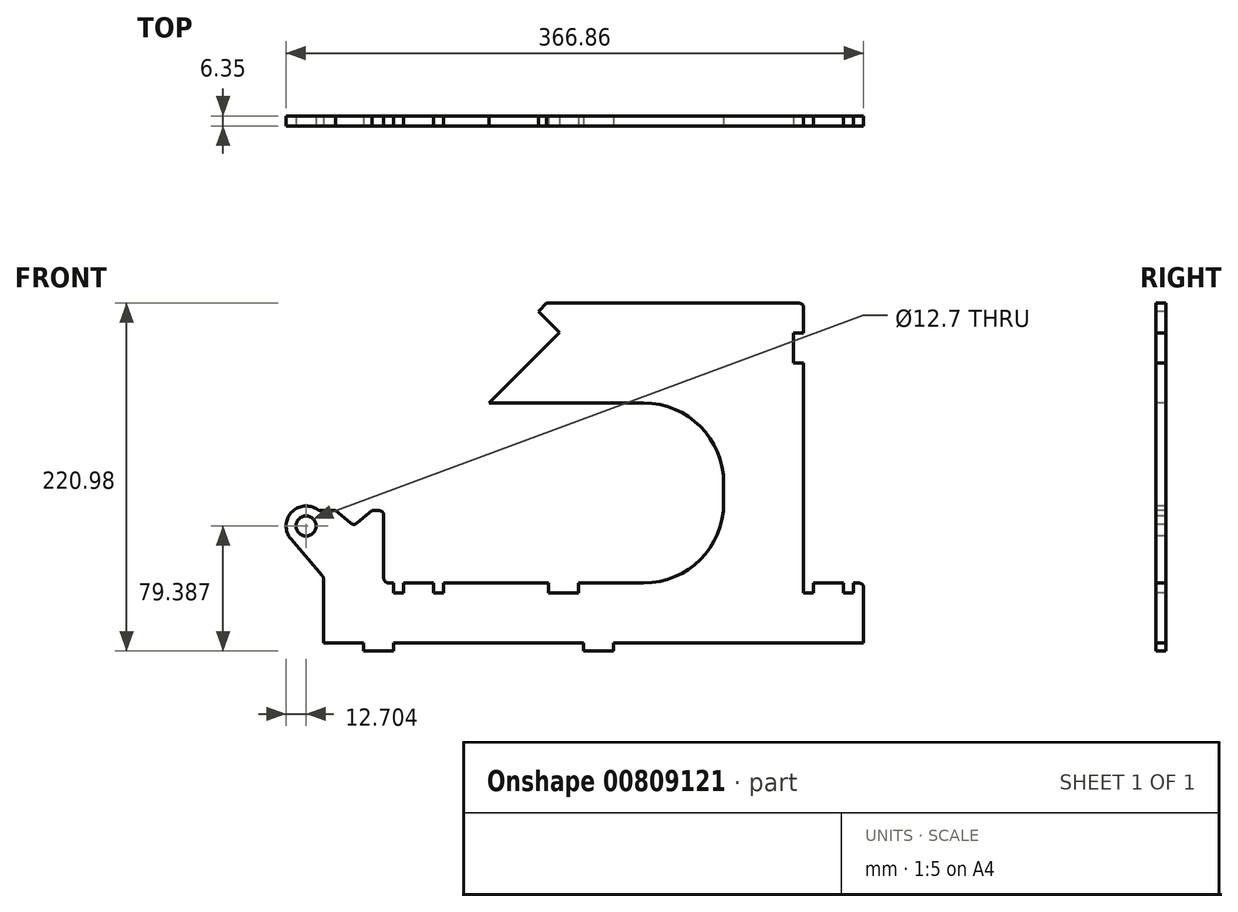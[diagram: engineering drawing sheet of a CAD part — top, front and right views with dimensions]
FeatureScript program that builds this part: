
annotation { "Feature Type Name" : "Feature", "Feature Type Description" : "" }
export const myFeature = defineFeature(function(context is Context, id is Id, definition is map)
    precondition{}
    {
        {
            var Q0;
            Q0=qCreatedBy(makeId("Front.planeOp"),FACE);
            var sketch = newSketch(context, id + "F0", { "sketchPlane" : qUnion([Q0])});
            skCircle(sketch, "E0", {"center": v(-91.4, -60.1) * mm, "radius": 6.35 * mm});
            skArc(sketch, "E1", {"start": v(-83.36, -50.27) * mm, "mid": v(-100.48, -51.22) * mm, "end": v(-101.06, -68.36) * mm});
            skLineSegment(sketch, "E2", {"start": v(-101.06, -68.36) * mm, "end": v(-80.15, -92.8) * mm});
            skLineSegment(sketch, "E3.trimOffspring", {"start": v(-80.15, -92.8) * mm, "end": v(-80.15, -134.4) * mm});
            skCircle(sketch, "E4", {"center": v(-61.1, -45.5) * mm, "radius": 11.11 * mm, "construction": true});
            skLineSegment(sketch, "E5.0", {"start": v(-83.36, -50.27) * mm, "end": v(-72.7, -50.27) * mm});
            skLineSegment(sketch, "E6", {"start": v(-42.05, -50.27) * mm, "end": v(-42.05, -96.3) * mm});
            skLineSegment(sketch, "E7.trimOffspring", {"start": v(-49.48, -50.27) * mm, "end": v(-42.05, -50.27) * mm});
            skPoint(sketch, "E8.orphan", {"position": v(-61.1, -63.47) * mm});
            skLineSegment(sketch, "E9.0", {"start": v(-72.7, -50.27) * mm, "end": v(-61.1, -60.02) * mm});
            skLineSegment(sketch, "E10.0", {"start": v(-49.48, -50.27) * mm, "end": v(-61.1, -60.02) * mm});
            skLineSegment(sketch, "E11", {"start": v(-68.24, -54.02) * mm, "end": v(-61.1, -45.5) * mm, "construction": true});
            skLineSegment(sketch, "E12", {"start": v(-53.95, -54.02) * mm, "end": v(-61.1, -45.5) * mm, "construction": true});
            skLineSegment(sketch, "E13.0", {"start": v(-42.05, -96.3) * mm, "end": v(-35.7, -96.3) * mm});
            skLineSegment(sketch, "E14.0", {"start": v(-80.15, -134.4) * mm, "end": v(262.75, -134.4) * mm});
            skLineSegment(sketch, "E15", {"start": v(-61.1, -45.5) * mm, "end": v(-34.5, -18.92) * mm, "construction": true});
            skLineSegment(sketch, "E16.0", {"start": v(-60.66, -29.36) * mm, "end": v(50.47, 81.77) * mm, "construction": true});
            skLineSegment(sketch, "E17", {"start": v(-61.1, -45.5) * mm, "end": v(-68.95, -37.65) * mm});
            skLineSegment(sketch, "E18.0", {"start": v(-53.24, -37.65) * mm, "end": v(-61.1, -29.8) * mm, "construction": true});
            skLineSegment(sketch, "E19.0", {"start": v(69.55, 62.69) * mm, "end": v(56.08, 76.16) * mm});
            skLineSegment(sketch, "E20.0", {"start": v(-52.8, -37.22) * mm, "end": v(-60.66, -29.36) * mm, "construction": true});
            skLineSegment(sketch, "E21.0", {"start": v(-63.34, -43.26) * mm, "end": v(50.52, 70.6) * mm, "construction": true});
            skLineSegment(sketch, "E22.0", {"start": v(173.85, -32.8) * mm, "end": v(173.85, -45.5) * mm});
            skLineSegment(sketch, "E23.0", {"start": v(61.41, 81.5) * mm, "end": v(224.65, 81.5) * mm});
            skLineSegment(sketch, "E24.0", {"start": v(6.9, 18) * mm, "end": v(24.85, 18) * mm, "construction": true});
            skLineSegment(sketch, "E25.0", {"start": v(224.65, 81.5) * mm, "end": v(224.65, 62.44) * mm});
            skLineSegment(sketch, "E26.0", {"start": v(-23.62, -12.52) * mm, "end": v(6.9, 18) * mm, "construction": true});
            skLineSegment(sketch, "E27.0", {"start": v(-23.62, -12.52) * mm, "end": v(-28.11, -8.03) * mm, "construction": true});
            skLineSegment(sketch, "E28", {"start": v(56.08, 76.16) * mm, "end": v(61.41, 81.5) * mm});
            skLineSegment(sketch, "E29", {"start": v(6.9, 18) * mm, "end": v(60.57, 71.67) * mm, "construction": true});
            skLineSegment(sketch, "E30.top", {"start": v(-35.7, -102.66) * mm, "end": v(-29.35, -102.66) * mm});
            skLineSegment(sketch, "E30.left", {"start": v(-35.7, -96.3) * mm, "end": v(-35.7, -102.66) * mm});
            skLineSegment(sketch, "E30.right", {"start": v(-29.35, -96.3) * mm, "end": v(-29.35, -102.66) * mm});
            skLineSegment(sketch, "E31.bottom", {"start": v(-10.3, -102.66) * mm, "end": v(-3.95, -102.66) * mm});
            skLineSegment(sketch, "E31.left", {"start": v(-10.3, -102.66) * mm, "end": v(-10.3, -96.3) * mm});
            skLineSegment(sketch, "E31.right", {"start": v(-3.95, -102.66) * mm, "end": v(-3.95, -96.3) * mm});
            skLineSegment(sketch, "E32.trimOffspring", {"start": v(-29.35, -96.3) * mm, "end": v(-10.3, -96.3) * mm});
            skLineSegment(sketch, "E33.trimOffspring", {"start": v(-3.95, -96.3) * mm, "end": v(123.05, -96.3) * mm});
            skLineSegment(sketch, "E34.top", {"start": v(224.65, 62.44) * mm, "end": v(218.3, 62.44) * mm});
            skLineSegment(sketch, "E35.bottom", {"start": v(218.3, 43.4) * mm, "end": v(224.65, 43.4) * mm});
            skLineSegment(sketch, "E35.left", {"start": v(218.3, 62.44) * mm, "end": v(218.3, 43.4) * mm});
            skLineSegment(sketch, "E36.trimOffspring", {"start": v(224.65, 43.4) * mm, "end": v(224.65, -102.66) * mm});
            skLineSegment(sketch, "E37.0", {"start": v(262.75, -96.3) * mm, "end": v(262.75, -134.4) * mm});
            skLineSegment(sketch, "E38.trimOffspring", {"start": v(231, -96.3) * mm, "end": v(250.05, -96.3) * mm});
            skLineSegment(sketch, "E39.top", {"start": v(224.65, -102.66) * mm, "end": v(231, -102.66) * mm});
            skLineSegment(sketch, "E39.right", {"start": v(231, -96.3) * mm, "end": v(231, -102.66) * mm});
            skLineSegment(sketch, "E40.top", {"start": v(250.05, -102.66) * mm, "end": v(256.4, -102.66) * mm});
            skLineSegment(sketch, "E40.left", {"start": v(250.05, -96.3) * mm, "end": v(250.05, -102.66) * mm});
            skLineSegment(sketch, "E40.right", {"start": v(256.4, -96.3) * mm, "end": v(256.4, -102.66) * mm});
            skLineSegment(sketch, "E41.trimOffspring", {"start": v(256.4, -96.3) * mm, "end": v(262.75, -96.3) * mm});
            skPoint(sketch, "E42.visualSharp", {"position": v(173.85, 18) * mm});
            skArc(sketch, "E42.filletArc", {"start": v(173.85, -32.8) * mm, "mid": v(158.97, 3.11) * mm, "end": v(123.05, 18) * mm});
            skPoint(sketch, "E43.visualSharp", {"position": v(173.85, -96.3) * mm});
            skArc(sketch, "E43.filletArc", {"start": v(123.05, -96.3) * mm, "mid": v(158.97, -81.43) * mm, "end": v(173.85, -45.5) * mm});
            skLineSegment(sketch, "E44.bottom", {"start": v(62.73, -102.66) * mm, "end": v(81.78, -102.66) * mm});
            skLineSegment(sketch, "E44.top", {"start": v(62.73, -96.3) * mm, "end": v(81.78, -96.3) * mm});
            skLineSegment(sketch, "E44.left", {"start": v(62.73, -102.66) * mm, "end": v(62.73, -96.3) * mm});
            skLineSegment(sketch, "E44.right", {"start": v(81.78, -102.66) * mm, "end": v(81.78, -96.3) * mm});
            skLineSegment(sketch, "E45.0", {"start": v(24.85, 18) * mm, "end": v(69.55, 62.69) * mm});
            skLineSegment(sketch, "E46", {"start": v(24.85, 18) * mm, "end": v(123.05, 18) * mm});
            skLineSegment(sketch, "E47.bottom", {"start": v(243.7, -134.4) * mm, "end": v(224.65, -134.4) * mm});
            skLineSegment(sketch, "E47.top", {"start": v(243.7, -139.49) * mm, "end": v(224.65, -139.49) * mm});
            skLineSegment(sketch, "E47.left", {"start": v(243.7, -134.4) * mm, "end": v(243.7, -139.49) * mm});
            skLineSegment(sketch, "E47.right", {"start": v(224.65, -134.4) * mm, "end": v(224.65, -139.49) * mm});
            skLineSegment(sketch, "E48.1.0.0", {"start": v(104, -139.49) * mm, "end": v(84.95, -139.49) * mm});
            skLineSegment(sketch, "E48.1.0.1", {"start": v(104, -134.4) * mm, "end": v(104, -139.49) * mm});
            skLineSegment(sketch, "E48.1.0.2", {"start": v(84.95, -134.4) * mm, "end": v(84.95, -139.49) * mm});
            skLineSegment(sketch, "E48.2.0.0", {"start": v(-35.7, -139.49) * mm, "end": v(-54.75, -139.49) * mm});
            skLineSegment(sketch, "E48.2.0.1", {"start": v(-35.7, -134.4) * mm, "end": v(-35.7, -139.49) * mm});
            skLineSegment(sketch, "E48.2.0.2", {"start": v(-54.75, -134.4) * mm, "end": v(-54.75, -139.49) * mm});
            skLineSegment(sketch, "E48.direction1", {"start": v(224.65, -139.49) * mm, "end": v(84.95, -139.49) * mm, "construction": true});
            skSolve(sketch);
        }
        {
            var Q0;
            Q0=makeQuery(id+"F0.imprint","IMPRINT",FACE,{"disambiguationData":[TD([[makeQuery(id+"F0.imprint","IMPRINT",EDGE,{"derivedFrom":sQuery(id+"F0.wireOp",EDGE,"E0")}),-1.0]])]});
            var Q1;
            Q1=makeQuery(id+"F0.imprint","IMPRINT",FACE,{"disambiguationData":[TD([[makeQuery(id+"F0.imprint","IMPRINT",EDGE,{"derivedFrom":sQuery(id+"F0.wireOp",EDGE,"E48.2.0.0")}),-1.0]])]});
            var Q2;
            Q2=makeQuery(id+"F0.imprint","IMPRINT",FACE,{"disambiguationData":[TD([[makeQuery(id+"F0.imprint","IMPRINT",EDGE,{"derivedFrom":sQuery(id+"F0.wireOp",EDGE,"E48.1.0.0")}),-1.0]])]});
            var Q3;
            Q3=makeQuery(id+"F0.imprint","IMPRINT",FACE,{"disambiguationData":[TD([[makeQuery(id+"F0.imprint","IMPRINT",EDGE,{"derivedFrom":sQuery(id+"F0.wireOp",EDGE,"E47.bottom")}),1.0]])]});
            extrude(context, id + "F1", {"entities" : qUnion([Q0, Q1, Q2, Q3]), "oppositeDirection" : true, "depth" : 6.35 * mm, "offsetDistance" : 25.4 * mm});
        }
        {
            var Q0;
            Q0=makeQuery(id+"F1.opExtrude","SWEPT_EDGE",EDGE,{"disambiguationData":[OSD([sQuery(id+"F0.wireOp",EDGE,"E23.0"),sQuery(id+"F0.wireOp",EDGE,"E25.0")])]});
            var Q1;
            Q1=makeQuery(id+"F1.opExtrude","SWEPT_EDGE",EDGE,{"disambiguationData":[OSD([sQuery(id+"F0.wireOp",EDGE,"E6"),sQuery(id+"F0.wireOp",EDGE,"E13.0")])]});
            fillet(context, id + "F2", {"entities" : qUnion([Q0, Q1]), "radius" : 3.17 * mm, "tangentPropagation" : true, "allowEdgeOverflow" : false});
        }
        {
            var Q0;
            Q0=makeQuery(id+"F1.opExtrude","SWEPT_EDGE",EDGE,{"disambiguationData":[OSD([sQuery(id+"F0.wireOp",EDGE,"E2"),sQuery(id+"F0.wireOp",EDGE,"E3.trimOffspring")])]});
            fillet(context, id + "F3", {"entities" : qUnion([Q0]), "radius" : 5.08 * mm, "tangentPropagation" : true, "allowEdgeOverflow" : false});
        }
        {
            var Q0;
            Q0=makeQuery(id+"F1.opExtrude","SWEPT_EDGE",EDGE,{"disambiguationData":[OSD([sQuery(id+"F0.wireOp",EDGE,"E6"),sQuery(id+"F0.wireOp",EDGE,"E7.trimOffspring")])]});
            fillet(context, id + "F4", {"entities" : qUnion([Q0]), "radius" : 3.17 * mm, "tangentPropagation" : true, "allowEdgeOverflow" : false});
        }
        {
            var Q0;
            Q0=makeQuery(id+"F1.opExtrude","SWEPT_EDGE",EDGE,{"disambiguationData":[OSD([sQuery(id+"F0.wireOp",EDGE,"E9.0"),sQuery(id+"F0.wireOp",EDGE,"E10.0")])]});
            var Q1;
            Q1=makeQuery(id+"F1.opExtrude","SWEPT_EDGE",EDGE,{"disambiguationData":[OSD([sQuery(id+"F0.wireOp",EDGE,"E1"),sQuery(id+"F0.wireOp",EDGE,"E5.0")])]});
            var Q2;
            Q2=makeQuery(id+"F1.opExtrude","SWEPT_EDGE",EDGE,{"disambiguationData":[OSD([sQuery(id+"F0.wireOp",EDGE,"E37.0"),sQuery(id+"F0.wireOp",EDGE,"E41.trimOffspring")])]});
            fillet(context, id + "F5", {"entities" : qUnion([Q0, Q1, Q2]), "radius" : 3.17 * mm, "tangentPropagation" : true, "allowEdgeOverflow" : false});
        }
    });
